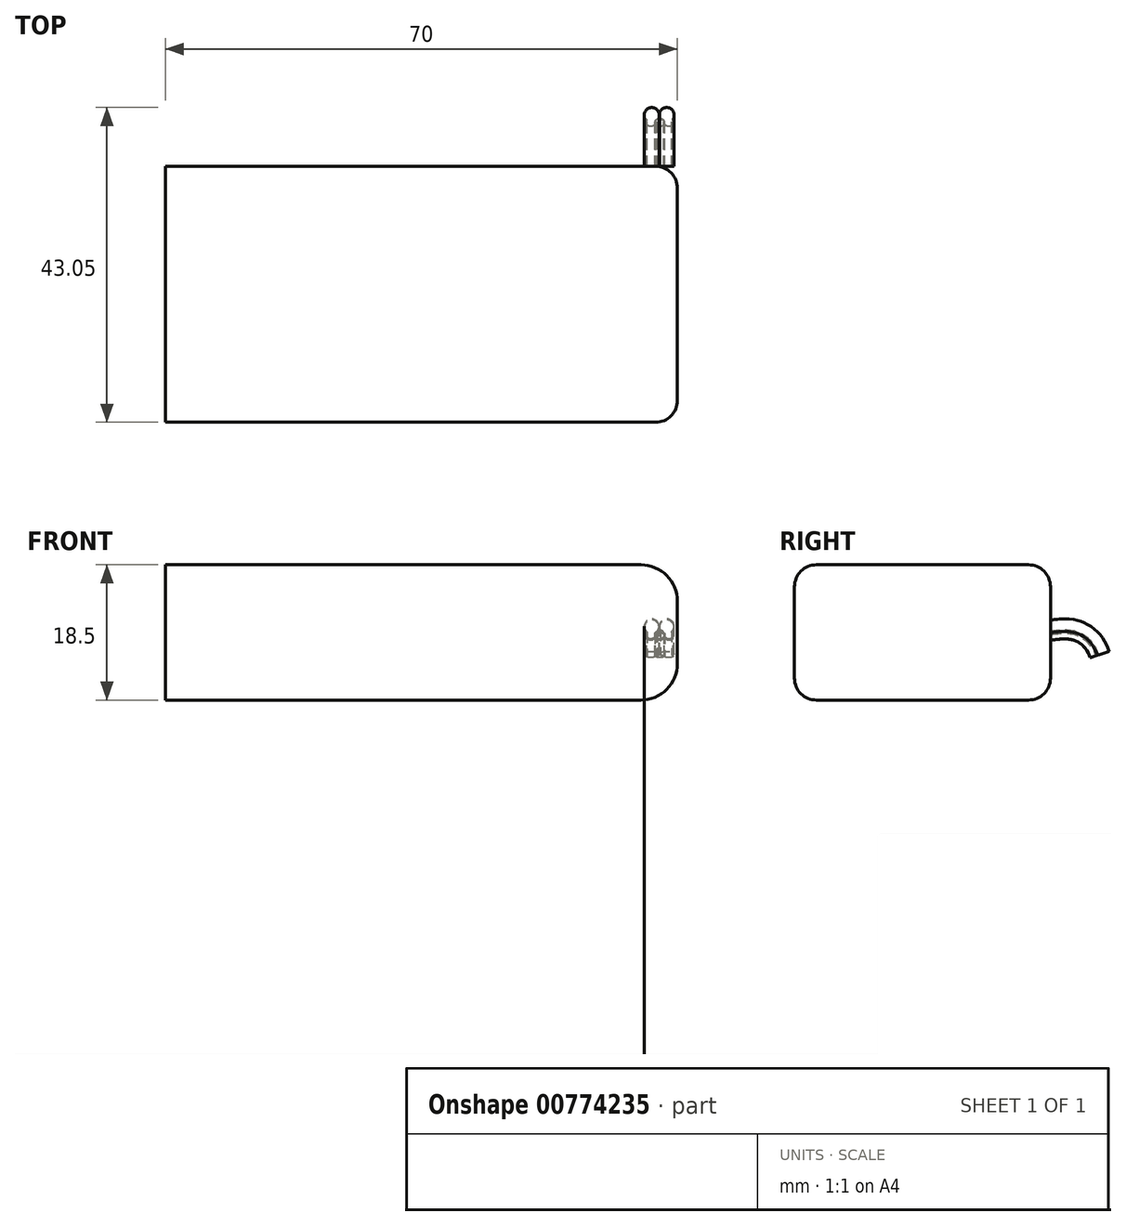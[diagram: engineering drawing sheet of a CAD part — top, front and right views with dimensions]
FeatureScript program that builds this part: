
annotation { "Feature Type Name" : "Feature", "Feature Type Description" : "" }
export const myFeature = defineFeature(function(context is Context, id is Id, definition is map)
    precondition{}
    {
        {
            assignVariable(context, id + "F0", {"name" : "D", "anyValue" : 18.5});
        }
        {
            var Q0;
            Q0=qCreatedBy(makeId("Top.planeOp"),FACE);
            var sketch = newSketch(context, id + "F1", { "sketchPlane" : qUnion([Q0])});
            skLineSegment(sketch, "E0.bottom", {"start": v(58.14, 30.54) * mm, "end": v(-11.86, 30.54) * mm});
            skLineSegment(sketch, "E0.top", {"start": v(58.14, -4.46) * mm, "end": v(-11.86, -4.46) * mm});
            skLineSegment(sketch, "E0.left", {"start": v(58.14, 30.54) * mm, "end": v(58.14, -4.46) * mm});
            skLineSegment(sketch, "E0.right", {"start": v(-11.86, 30.54) * mm, "end": v(-11.86, -4.46) * mm});
            skSolve(sketch);
        }
        {
            var Q0;
            Q0 = qSketchRegion(id + "F1", true);
            extrude(context, id + "F2", {"entities" : qUnion([Q0]), "depth" : (getVariable(context, 'D')) * mm, "offsetDistance" : 25 * mm});
        }
        {
            var Q0;
            Q0=makeQuery(id+"F2.opExtrude","CAP_EDGE",EDGE,{"disambiguationData":[OSD([sQuery(id+"F1.wireOp",EDGE,"E0.left")])],"isStart":false});
            var Q1;
            Q1=makeQuery(id+"F2.opExtrude","CAP_EDGE",EDGE,{"disambiguationData":[OSD([sQuery(id+"F1.wireOp",EDGE,"E0.left")])],"isStart":true});
            fillet(context, id + "F3", {"entities" : qUnion([Q0, Q1]), "radius" : 5 * mm, "tangentPropagation" : true, "allowEdgeOverflow" : false});
        }
        {
            var Q0;
            Q0=makeQuery(id+"F2.opExtrude","SWEPT_FACE",FACE,{"disambiguationData":[OSD([sQuery(id+"F1.wireOp",EDGE,"E0.bottom")])]});
            var sketch = newSketch(context, id + "F4", { "sketchPlane" : qUnion([Q0])});
            skLineSegment(sketch, "E1", {"start": v(-56.67, 9.96) * mm, "end": v(-42.7, 9.96) * mm, "construction": true});
            skPoint(sketch, "E1.startSnap0", {"position": v(-56.67, 17.04) * mm});
            skCircle(sketch, "E2", {"center": v(-56.67, 9.96) * mm, "radius": 1 * mm});
            skCircle(sketch, "E3", {"center": v(-54.62, 9.96) * mm, "radius": 1 * mm});
            skCircle(sketch, "E4", {"center": v(-56.96, 8.82) * mm, "radius": 0.6 * mm});
            skLineSegment(sketch, "E5", {"start": v(-56.96, 8.82) * mm, "end": v(-44.78, 8.82) * mm, "construction": true});
            skCircle(sketch, "E6", {"center": v(-55.73, 8.82) * mm, "radius": 0.6 * mm});
            skCircle(sketch, "E7", {"center": v(-54.49, 8.82) * mm, "radius": 0.6 * mm});
            skSolve(sketch);
        }
        {
            var Q0;
            Q0=makeQuery(id+"F2.opExtrude","SWEPT_FACE",FACE,{"disambiguationData":[OSD([sQuery(id+"F1.wireOp",EDGE,"E0.left")])]});
            var sketch = newSketch(context, id + "F5", { "sketchPlane" : qUnion([Q0])});
            skFitSpline(sketch, "E8", {"points": [v(30.58, 7.48) * mm, v(35.3, 5.53) * mm], "startDerivative": vector(4.8, 0.18) * mm, "endDerivative": vector(3.09, -8.3) * mm});
            skSolve(sketch);
        }
        {
            var Q0;
            Q0=makeQuery(id+"F4.imprint","IMPRINT",FACE,{"disambiguationData":[TD([[makeQuery(id+"F4.imprint","IMPRINT",EDGE,{"derivedFrom":sQuery(id+"F4.wireOp",EDGE,"E7")}),1.0]])]});
            var Q1;
            {var subQ0=sQuery(id+"F4.wireOp",EDGE,"E6");var subQ1=makeQuery(id+"F4.imprint","INTERSECT",VERTEX,{"derivedFrom":[sQuery(id+"F4.wireOp",EDGE,"E4"),subQ0]});Q1=makeQuery(id+"F4.imprint","IMPRINT",FACE,{"disambiguationData":[TD([[makeQuery(id+"F4.imprint","IMPRINT",EDGE,{"disambiguationData":[TD([[subQ1,1.0]])],"derivedFrom":subQ0}),1.0]])]});}
            var Q2;
            Q2=makeQuery(id+"F4.imprint","IMPRINT",FACE,{"disambiguationData":[TD([[makeQuery(id+"F4.imprint","IMPRINT",EDGE,{"derivedFrom":sQuery(id+"F4.wireOp",EDGE,"E4")}),1.0]])]});
            var Q3;
            Q3=makeQuery(id+"F4.imprint","IMPRINT",FACE,{"disambiguationData":[TD([[makeQuery(id+"F4.imprint","IMPRINT",EDGE,{"derivedFrom":sQuery(id+"F4.wireOp",EDGE,"E3")}),1.0]])]});
            var Q4;
            Q4=makeQuery(id+"F4.imprint","IMPRINT",FACE,{"disambiguationData":[TD([[makeQuery(id+"F4.imprint","IMPRINT",EDGE,{"derivedFrom":sQuery(id+"F4.wireOp",EDGE,"E2")}),1.0]])]});
            var Q5;
            Q5=sQuery(id+"F5.wireOp",EDGE,"E8");
            sweep(context, id + "F6", {"profiles" : qUnion([Q0, Q1, Q2, Q3, Q4]), "path" : qUnion([Q5])});
        }
        {
            var Q0;
            Q0=makeQuery(id+"F2.opExtrude","CAP_EDGE",EDGE,{"disambiguationData":[OSD([sQuery(id+"F1.wireOp",EDGE,"E0.bottom")])],"isStart":false});
            var Q1;
            Q1=makeQuery(id+"F2.opExtrude","CAP_EDGE",EDGE,{"disambiguationData":[OSD([sQuery(id+"F1.wireOp",EDGE,"E0.top")])],"isStart":false});
            var Q2;
            Q2=makeQuery(id+"F2.opExtrude","CAP_EDGE",EDGE,{"disambiguationData":[OSD([sQuery(id+"F1.wireOp",EDGE,"E0.top")])],"isStart":true});
            fillet(context, id + "F7", {"entities" : qUnion([Q0, Q1, Q2]), "radius" : 3 * mm, "tangentPropagation" : true, "allowEdgeOverflow" : false});
        }
    });
